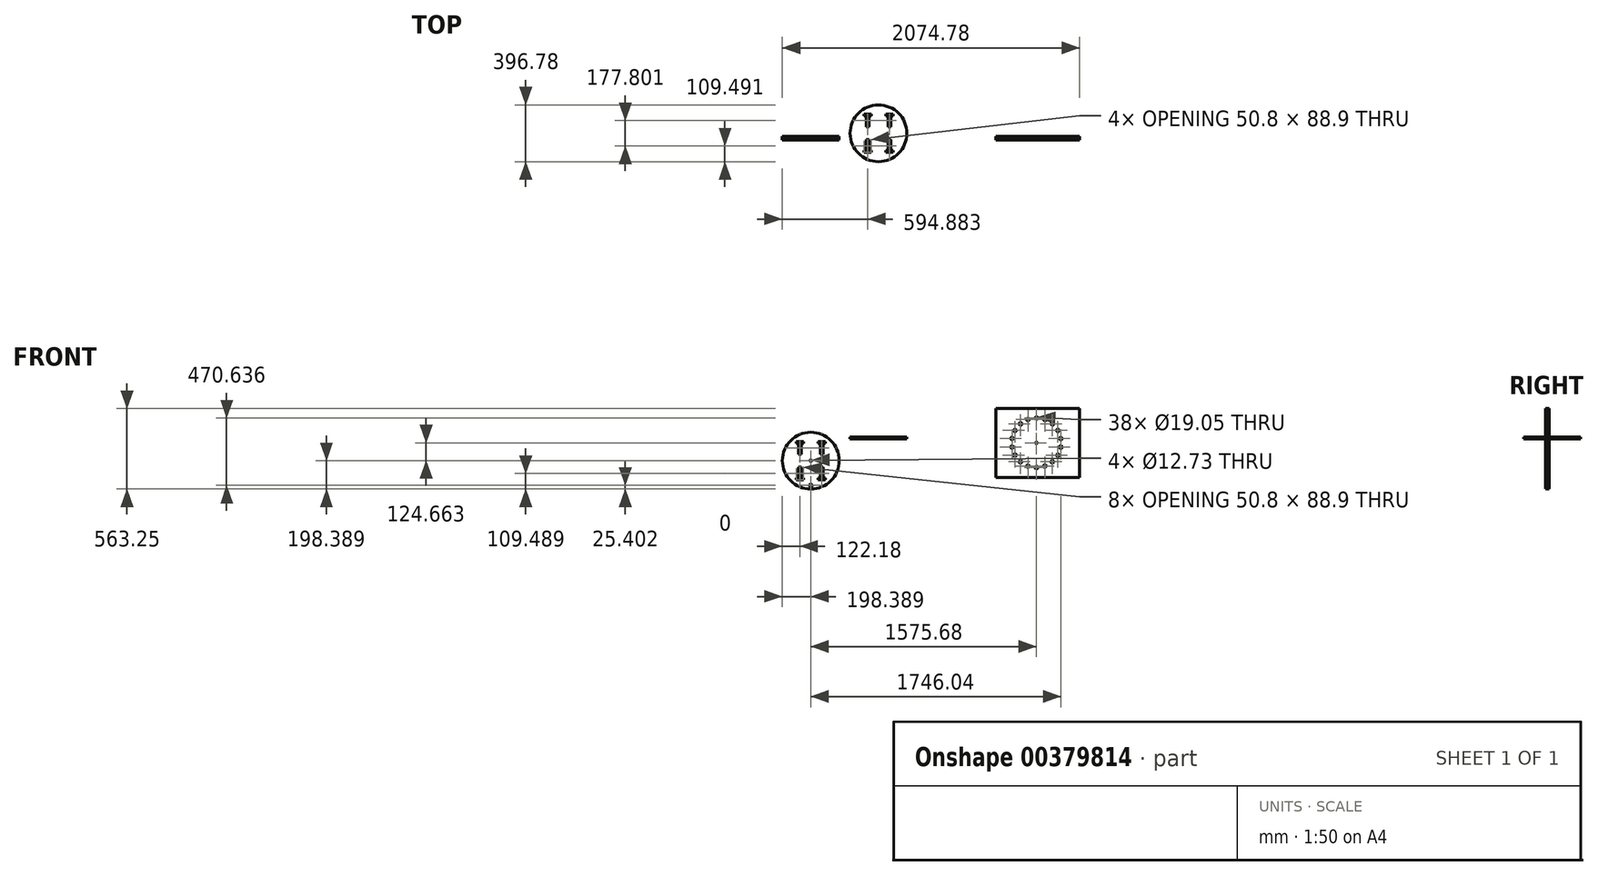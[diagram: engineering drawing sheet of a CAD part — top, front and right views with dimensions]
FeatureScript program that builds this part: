
annotation { "Feature Type Name" : "Feature", "Feature Type Description" : "" }
export const myFeature = defineFeature(function(context is Context, id is Id, definition is map)
    precondition{}
    {
        {
            var Q0;
            Q0=qCreatedBy(makeId("Top.planeOp"),FACE);
            var sketch = newSketch(context, id + "F0", { "sketchPlane" : qUnion([Q0])});
            skCircle(sketch, "E0", {"center": v(-50.8, 20.68) * mm, "radius": 198.39 * mm});
            skLineSegment(sketch, "E1", {"start": v(-50.8, 219.07) * mm, "end": v(-50.8, -177.7) * mm, "construction": true});
            skLineSegment(sketch, "E2", {"start": v(-249.2, 20.68) * mm, "end": v(147.58, 20.68) * mm, "construction": true});
            skLineSegment(sketch, "E3", {"start": v(-203.22, -106.32) * mm, "end": v(101.6, -106.32) * mm, "construction": true});
            skLineSegment(sketch, "E4", {"start": v(-203.22, 147.68) * mm, "end": v(101.6, 147.68) * mm, "construction": true});
            skPoint(sketch, "E5", {"position": v(-152.42, -106.32) * mm});
            skPoint(sketch, "E6", {"position": v(-101.62, -106.32) * mm});
            skPoint(sketch, "E7", {"position": v(0, -106.32) * mm});
            skPoint(sketch, "E8", {"position": v(50.8, -106.32) * mm});
            skPoint(sketch, "E9", {"position": v(50.8, 147.68) * mm});
            skPoint(sketch, "E10", {"position": v(0, 147.68) * mm});
            skPoint(sketch, "E11", {"position": v(-101.62, 147.68) * mm});
            skPoint(sketch, "E12", {"position": v(-152.42, 147.68) * mm});
            skLineSegment(sketch, "E13", {"start": v(-152.42, -106.32) * mm, "end": v(-152.42, -99.97) * mm});
            skLineSegment(sketch, "E14", {"start": v(-152.42, -99.97) * mm, "end": v(-101.7, -99.97) * mm});
            skLineSegment(sketch, "E15", {"start": v(-101.7, -99.97) * mm, "end": v(-101.62, -106.32) * mm});
            skLineSegment(sketch, "E16", {"start": v(-101.62, -106.32) * mm, "end": v(-101.62, -112.67) * mm});
            skLineSegment(sketch, "E17", {"start": v(-101.62, -112.67) * mm, "end": v(-152.42, -112.67) * mm});
            skLineSegment(sketch, "E18", {"start": v(-152.42, -112.67) * mm, "end": v(-152.42, -106.32) * mm});
            skLineSegment(sketch, "E19", {"start": v(0, -106.32) * mm, "end": v(0, -99.97) * mm});
            skLineSegment(sketch, "E20", {"start": v(0, -99.97) * mm, "end": v(50.8, -99.97) * mm});
            skLineSegment(sketch, "E21", {"start": v(50.8, -99.97) * mm, "end": v(50.8, -106.32) * mm});
            skLineSegment(sketch, "E22", {"start": v(50.8, -112.67) * mm, "end": v(0, -112.67) * mm});
            skLineSegment(sketch, "E23", {"start": v(0, -112.67) * mm, "end": v(0, -106.32) * mm});
            skLineSegment(sketch, "E24", {"start": v(0, 147.68) * mm, "end": v(0, 154.03) * mm});
            skLineSegment(sketch, "E25", {"start": v(0, 154.03) * mm, "end": v(50.8, 154.03) * mm});
            skLineSegment(sketch, "E26", {"start": v(50.8, 154.03) * mm, "end": v(50.8, 147.68) * mm});
            skLineSegment(sketch, "E27", {"start": v(50.8, 147.68) * mm, "end": v(50.8, 141.33) * mm});
            skLineSegment(sketch, "E28", {"start": v(50.8, 141.33) * mm, "end": v(0, 141.33) * mm});
            skLineSegment(sketch, "E29", {"start": v(0, 141.33) * mm, "end": v(0, 147.68) * mm});
            skLineSegment(sketch, "E30", {"start": v(-152.42, 147.68) * mm, "end": v(-152.42, 141.33) * mm});
            skLineSegment(sketch, "E31", {"start": v(-152.42, 141.33) * mm, "end": v(-101.62, 141.33) * mm});
            skLineSegment(sketch, "E32", {"start": v(-101.62, 141.33) * mm, "end": v(-101.62, 147.68) * mm});
            skLineSegment(sketch, "E33", {"start": v(-101.62, 147.68) * mm, "end": v(-101.62, 154.03) * mm});
            skLineSegment(sketch, "E34", {"start": v(-101.62, 154.03) * mm, "end": v(-152.42, 154.03) * mm});
            skLineSegment(sketch, "E35", {"start": v(-152.42, 154.03) * mm, "end": v(-152.42, 147.68) * mm});
            skLineSegment(sketch, "E36", {"start": v(50.8, -106.32) * mm, "end": v(50.8, -112.67) * mm});
            skLineSegment(sketch, "E37", {"start": v(-127.06, -99.97) * mm, "end": v(-127.06, -23.77) * mm, "construction": true});
            skLineSegment(sketch, "E38", {"start": v(-127.06, -23.77) * mm, "end": v(-136.58, -23.77) * mm});
            skLineSegment(sketch, "E39", {"start": v(-127.06, -23.77) * mm, "end": v(-117.53, -23.77) * mm});
            skLineSegment(sketch, "E40", {"start": v(-136.58, -23.77) * mm, "end": v(-136.58, -99.97) * mm});
            skLineSegment(sketch, "E41", {"start": v(-117.53, -23.77) * mm, "end": v(-117.53, -99.97) * mm});
            skLineSegment(sketch, "E42.MirrorCS", {"start": v(15.92, -23.77) * mm, "end": v(15.92, -99.97) * mm});
            skLineSegment(sketch, "E43.MirrorCS", {"start": v(25.44, -23.77) * mm, "end": v(15.92, -23.77) * mm});
            skLineSegment(sketch, "E44.MirrorCS", {"start": v(25.44, -23.77) * mm, "end": v(34.97, -23.77) * mm});
            skLineSegment(sketch, "E45.MirrorCS", {"start": v(34.97, -23.77) * mm, "end": v(34.97, -99.97) * mm});
            skLineSegment(sketch, "E46.MirrorCS", {"start": v(-127.06, 65.13) * mm, "end": v(-117.53, 65.13) * mm});
            skLineSegment(sketch, "E47.MirrorCS", {"start": v(-117.53, 65.13) * mm, "end": v(-117.53, 141.33) * mm});
            skLineSegment(sketch, "E48.MirrorCS", {"start": v(-136.58, 65.13) * mm, "end": v(-136.58, 141.33) * mm});
            skLineSegment(sketch, "E49.MirrorCS", {"start": v(-127.06, 65.13) * mm, "end": v(-136.58, 65.13) * mm});
            skLineSegment(sketch, "E50.MirrorCS", {"start": v(25.44, 65.13) * mm, "end": v(15.92, 65.13) * mm});
            skLineSegment(sketch, "E51.MirrorCS", {"start": v(25.44, 65.13) * mm, "end": v(34.97, 65.13) * mm});
            skLineSegment(sketch, "E52.MirrorCS", {"start": v(34.97, 65.13) * mm, "end": v(34.97, 141.33) * mm});
            skLineSegment(sketch, "E53.MirrorCS", {"start": v(15.92, 65.13) * mm, "end": v(15.92, 141.33) * mm});
            skSolve(sketch);
        }
        {
            var Q0;
            Q0=makeQuery(id+"F0.imprint","IMPRINT",FACE,{"disambiguationData":[TD([[makeQuery(id+"F0.imprint","IMPRINT",EDGE,{"derivedFrom":sQuery(id+"F0.wireOp",EDGE,"E0")}),1.0]])]});
            extrude(context, id + "F1", {"entities" : qUnion([Q0]), "depth" : 12.7 * mm});
        }
        {
            var Q0;
            Q0=qCreatedBy(makeId("Front.planeOp"),FACE);
            var sketch = newSketch(context, id + "F2", { "sketchPlane" : qUnion([Q0])});
            skCircle(sketch, "E54", {"center": v(-523.51, -151) * mm, "radius": 198.39 * mm});
            skLineSegment(sketch, "E55", {"start": v(-523.51, 47.4) * mm, "end": v(-523.51, -349.38) * mm, "construction": true});
            skLineSegment(sketch, "E56", {"start": v(-721.9, -151) * mm, "end": v(-325.12, -151) * mm, "construction": true});
            skLineSegment(sketch, "E57", {"start": v(-675.92, -278) * mm, "end": v(-371.1, -278) * mm, "construction": true});
            skLineSegment(sketch, "E58", {"start": v(-675.92, -24) * mm, "end": v(-371.1, -24) * mm, "construction": true});
            skPoint(sketch, "E59", {"position": v(-625.12, -278) * mm});
            skPoint(sketch, "E60", {"position": v(-574.32, -278) * mm});
            skPoint(sketch, "E61", {"position": v(-472.7, -278) * mm});
            skPoint(sketch, "E62", {"position": v(-421.9, -278) * mm});
            skPoint(sketch, "E63", {"position": v(-421.9, -24) * mm});
            skPoint(sketch, "E64", {"position": v(-472.7, -24) * mm});
            skPoint(sketch, "E65", {"position": v(-574.32, -24) * mm});
            skPoint(sketch, "E66", {"position": v(-625.12, -24) * mm});
            skLineSegment(sketch, "E67", {"start": v(-625.12, -278) * mm, "end": v(-625.12, -271.64) * mm});
            skLineSegment(sketch, "E68", {"start": v(-625.12, -271.64) * mm, "end": v(-574.4, -271.64) * mm});
            skLineSegment(sketch, "E69", {"start": v(-574.4, -271.64) * mm, "end": v(-574.32, -278) * mm});
            skLineSegment(sketch, "E70", {"start": v(-574.32, -278) * mm, "end": v(-574.32, -284.34) * mm});
            skLineSegment(sketch, "E71", {"start": v(-574.32, -284.34) * mm, "end": v(-625.12, -284.34) * mm});
            skLineSegment(sketch, "E72", {"start": v(-625.12, -284.34) * mm, "end": v(-625.12, -278) * mm});
            skLineSegment(sketch, "E73", {"start": v(-472.7, -278) * mm, "end": v(-472.7, -271.64) * mm});
            skLineSegment(sketch, "E74", {"start": v(-472.7, -271.64) * mm, "end": v(-421.9, -271.64) * mm});
            skLineSegment(sketch, "E75", {"start": v(-421.9, -271.64) * mm, "end": v(-421.9, -278) * mm});
            skLineSegment(sketch, "E76", {"start": v(-421.9, -284.34) * mm, "end": v(-472.7, -284.34) * mm});
            skLineSegment(sketch, "E77", {"start": v(-472.7, -284.34) * mm, "end": v(-472.7, -278) * mm});
            skLineSegment(sketch, "E78", {"start": v(-472.7, -24) * mm, "end": v(-472.7, -17.64) * mm});
            skLineSegment(sketch, "E79", {"start": v(-472.7, -17.64) * mm, "end": v(-421.9, -17.64) * mm});
            skLineSegment(sketch, "E80", {"start": v(-421.9, -17.64) * mm, "end": v(-421.9, -24) * mm});
            skLineSegment(sketch, "E81", {"start": v(-421.9, -24) * mm, "end": v(-421.9, -30.34) * mm});
            skLineSegment(sketch, "E82", {"start": v(-421.9, -30.34) * mm, "end": v(-472.7, -30.34) * mm});
            skLineSegment(sketch, "E83", {"start": v(-472.7, -30.34) * mm, "end": v(-472.7, -24) * mm});
            skLineSegment(sketch, "E84", {"start": v(-625.12, -24) * mm, "end": v(-625.12, -30.34) * mm});
            skLineSegment(sketch, "E85", {"start": v(-625.12, -30.34) * mm, "end": v(-574.32, -30.34) * mm});
            skLineSegment(sketch, "E86", {"start": v(-574.32, -30.34) * mm, "end": v(-574.32, -24) * mm});
            skLineSegment(sketch, "E87", {"start": v(-574.32, -24) * mm, "end": v(-574.32, -17.64) * mm});
            skLineSegment(sketch, "E88", {"start": v(-574.32, -17.64) * mm, "end": v(-625.12, -17.64) * mm});
            skLineSegment(sketch, "E89", {"start": v(-625.12, -17.64) * mm, "end": v(-625.12, -24) * mm});
            skLineSegment(sketch, "E90", {"start": v(-421.9, -278) * mm, "end": v(-421.9, -284.34) * mm});
            skLineSegment(sketch, "E91", {"start": v(-599.76, -271.64) * mm, "end": v(-599.76, -195.44) * mm, "construction": true});
            skLineSegment(sketch, "E92", {"start": v(-599.76, -195.44) * mm, "end": v(-609.29, -195.44) * mm});
            skLineSegment(sketch, "E93", {"start": v(-599.76, -195.44) * mm, "end": v(-590.24, -195.44) * mm});
            skLineSegment(sketch, "E94", {"start": v(-609.29, -195.44) * mm, "end": v(-609.29, -271.64) * mm});
            skLineSegment(sketch, "E95", {"start": v(-590.24, -195.44) * mm, "end": v(-590.24, -271.64) * mm});
            skLineSegment(sketch, "E96.MirrorCS", {"start": v(-456.79, -195.44) * mm, "end": v(-456.79, -271.64) * mm});
            skLineSegment(sketch, "E97.MirrorCS", {"start": v(-447.26, -195.44) * mm, "end": v(-456.79, -195.44) * mm});
            skLineSegment(sketch, "E98.MirrorCS", {"start": v(-447.26, -195.44) * mm, "end": v(-437.74, -195.44) * mm});
            skLineSegment(sketch, "E99.MirrorCS", {"start": v(-437.74, -195.44) * mm, "end": v(-437.74, -271.64) * mm});
            skLineSegment(sketch, "E100.MirrorCS", {"start": v(-599.76, -106.54) * mm, "end": v(-590.24, -106.54) * mm});
            skLineSegment(sketch, "E101.MirrorCS", {"start": v(-590.24, -106.54) * mm, "end": v(-590.24, -30.34) * mm});
            skLineSegment(sketch, "E102.MirrorCS", {"start": v(-609.29, -106.54) * mm, "end": v(-609.29, -30.34) * mm});
            skLineSegment(sketch, "E103.MirrorCS", {"start": v(-599.76, -106.54) * mm, "end": v(-609.29, -106.54) * mm});
            skLineSegment(sketch, "E104.MirrorCS", {"start": v(-447.26, -106.54) * mm, "end": v(-456.79, -106.54) * mm});
            skLineSegment(sketch, "E105.MirrorCS", {"start": v(-447.26, -106.54) * mm, "end": v(-437.74, -106.54) * mm});
            skLineSegment(sketch, "E106.MirrorCS", {"start": v(-437.74, -106.54) * mm, "end": v(-437.74, -30.34) * mm});
            skLineSegment(sketch, "E107.MirrorCS", {"start": v(-456.79, -106.54) * mm, "end": v(-456.79, -30.34) * mm});
            skCircle(sketch, "E108", {"center": v(-523.51, -323.98) * mm, "radius": 9.53 * mm});
            skLineSegment(sketch, "E109.bottom", {"start": v(768.68, 213.87) * mm, "end": v(1352.88, 213.87) * mm});
            skLineSegment(sketch, "E109.top", {"start": v(768.68, -268.73) * mm, "end": v(1352.88, -268.73) * mm});
            skLineSegment(sketch, "E109.left", {"start": v(768.68, 213.87) * mm, "end": v(768.68, -268.73) * mm});
            skLineSegment(sketch, "E109.right", {"start": v(1352.88, 213.87) * mm, "end": v(1352.88, -268.73) * mm});
            skCircle(sketch, "E110", {"center": v(1052.17, -199.31) * mm, "radius": 9.53 * mm});
            skCircle(sketch, "E111.1.0", {"center": v(993, -188.88) * mm, "radius": 9.53 * mm});
            skCircle(sketch, "E111.2.0", {"center": v(940.98, -158.84) * mm, "radius": 9.53 * mm});
            skCircle(sketch, "E111.3.0", {"center": v(902.36, -112.82) * mm, "radius": 9.53 * mm});
            skCircle(sketch, "E111.4.0", {"center": v(881.82, -56.37) * mm, "radius": 9.53 * mm});
            skCircle(sketch, "E111.5.0", {"center": v(881.82, 3.71) * mm, "radius": 9.53 * mm});
            skCircle(sketch, "E111.6.0", {"center": v(902.36, 60.17) * mm, "radius": 9.53 * mm});
            skCircle(sketch, "E111.7.0", {"center": v(940.98, 106.19) * mm, "radius": 9.53 * mm});
            skCircle(sketch, "E111.8.0", {"center": v(993, 136.23) * mm, "radius": 9.53 * mm});
            skCircle(sketch, "E111.9.0", {"center": v(1052.17, 146.66) * mm, "radius": 9.53 * mm});
            skPoint(sketch, "E111.center", {"position": v(1052.17, -26.33) * mm});
            skLineSegment(sketch, "E111.anchor1", {"start": v(1052.17, -26.33) * mm, "end": v(1052.17, -199.31) * mm, "construction": true});
            skLineSegment(sketch, "E111.anchor2", {"start": v(1052.17, -26.33) * mm, "end": v(1052.17, 146.66) * mm, "construction": true});
            skCircle(sketch, "E112.1.0", {"center": v(1111.34, 136.23) * mm, "radius": 9.53 * mm});
            skCircle(sketch, "E112.2.0", {"center": v(1163.37, 106.19) * mm, "radius": 9.53 * mm});
            skCircle(sketch, "E112.3.0", {"center": v(1201.98, 60.17) * mm, "radius": 9.53 * mm});
            skCircle(sketch, "E112.4.0", {"center": v(1222.53, 3.71) * mm, "radius": 9.53 * mm});
            skCircle(sketch, "E112.5.0", {"center": v(1222.53, -56.37) * mm, "radius": 9.53 * mm});
            skCircle(sketch, "E112.6.0", {"center": v(1201.98, -112.82) * mm, "radius": 9.53 * mm});
            skCircle(sketch, "E112.7.0", {"center": v(1163.37, -158.84) * mm, "radius": 9.53 * mm});
            skCircle(sketch, "E112.8.0", {"center": v(1111.34, -188.88) * mm, "radius": 9.53 * mm});
            skCircle(sketch, "E113", {"center": v(-523.51, -151) * mm, "radius": 6.36 * mm});
            skCircle(sketch, "E114", {"center": v(1052.17, -26.33) * mm, "radius": 6.36 * mm});
            skSolve(sketch);
        }
        {
            var Q0;
            Q0 = qSketchRegion(id + "F2", true);
            extrude(context, id + "F3", {"entities" : qUnion([Q0]), "depth" : 25.4 * mm});
        }
        {
            var Q0;
            Q0 = qSketchRegion(id + "F2", true);
            extrude(context, id + "F4", {"entities" : qUnion([Q0]), "depth" : 19.05 * mm});
        }
    });
